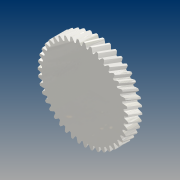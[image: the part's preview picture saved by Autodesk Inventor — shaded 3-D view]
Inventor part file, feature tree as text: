
AUTODESK INVENTOR PART (.ipt)
format: ipt  version: 2021 (Build 250183000, 183)  size: 660,992 bytes
history: native  units: mm (DEFAULTED — no unit token found)
features: extrude x3, plane x3, other x3, sketch x3
ambient origin geometry x8: Origin, YZ Plane, XZ Plane, XY Plane, X Axis, Y Axis, Z Axis, Center Point
bodies: Solid1 (feature_tree)
feature tree (12):
  extrude  "Extrusion1"  Depth=15.0mm TaperAngle=0.0deg
  plane  "Work Plane2"
  plane  "Work Plane8"
  plane  "Work Plane9"
  other  "Spur Gear"
  sketch  "Sketch3"  dims[d16=70.0mm d17=0.0mm d34=0.730603mm d39=0.0mm d41=0.0mm d43=70.0mm d46=70.0mm d47=0.0mm d48=0.0mm d49=10.0mm d50=5.0mm d51=17.0mm d52=0.0mm d53=10.0mm d54=0.0mm]
  extrude  "Extrusion2"  Depth=10.0mm TaperAngle=0.0deg
  extrude  "Extrusion3"  Depth=10.0mm TaperAngle=0.0deg
  sketch  "Sketch1"  dims[d0=97.176178mm d1=15.0mm d2=0.0mm]
  sketch  "Sketch2"  dims[d3=91.519288mm d4=10.0mm d5=0.0mm]
  other  "Srf1"
  other  "Pitch Diameter"
